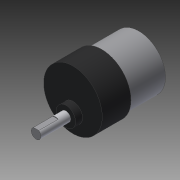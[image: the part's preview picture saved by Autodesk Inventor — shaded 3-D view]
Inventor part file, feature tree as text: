
AUTODESK INVENTOR PART (.ipt)
format: ipt  version: 2014 SP1 (Build 180222100, 222)  size: 164,864 bytes
history: native  units: in
note: dims shown in document units (in); Inventor stores cm internally (conversion verified against a paired STEP export)
features: extrude x7, sketch x7, thread x4
ambient origin geometry x8: Origin, YZ Plane, XZ Plane, XY Plane, X Axis, Y Axis, Z Axis, Center Point
bodies: Solid1 (feature_tree)
feature tree (18):
  extrude  "Extrusion1"  Depth=0.7in TaperAngle=0.0deg
  extrude  "Extrusion2"  Depth=0.47in
  extrude  "Extrusion3"  Depth=0.17in
  extrude  "Extrusion4"  Depth=0.4724in TaperAngle=0.0deg
  extrude  "Extrusion5"  Depth=0.9in TaperAngle=0.0deg
  extrude  "Extrusion6"  Depth=0.125in TaperAngle=0.0deg
  extrude  "Extrusion7"  Depth=0.1181in
  thread  "Thread1"  [1 undecoded]
  thread  "Thread2"  [1 undecoded]
  thread  "Thread3"  [1 undecoded]
  thread  "Thread4"  [1 undecoded]
  sketch  "Sketch1"  dims[d0=1.425in d1=0.7in d2=0.0in]
  sketch  "Sketch2"  dims[d3=0.449in d4=0.47in]
  sketch  "Sketch3"  dims[d5=0.17in d6=0.0in d7=0.2362in]
  sketch  "Sketch4"  dims[d8=0.725in d9=0.0in d11=0.4724in d12=0.0in]
  sketch  "Sketch5"  dims[d13=1.3in d14=0.9in d15=0.0in]
  sketch  "Sketch6"  dims[d16=0.35in d17=0.125in d18=0.0in]
  sketch  "Sketch7"  dims[d21=0.1181in d22=0.1181in d23=2.114in d24=2.114in d25=0.1181in d26=0.1181in d27=0.5in d28=0.0in d29=1.0in d30=0.0in d31=1.0in d32=0.0in d33=1.0in d34=0.0in d35=1.0in d36=0.0in]
note: 4 required parameter values undecoded (feature->parameter linkage not recoverable at this tier; creation-order binding heuristic only, values carry confidence <= 0.55)
